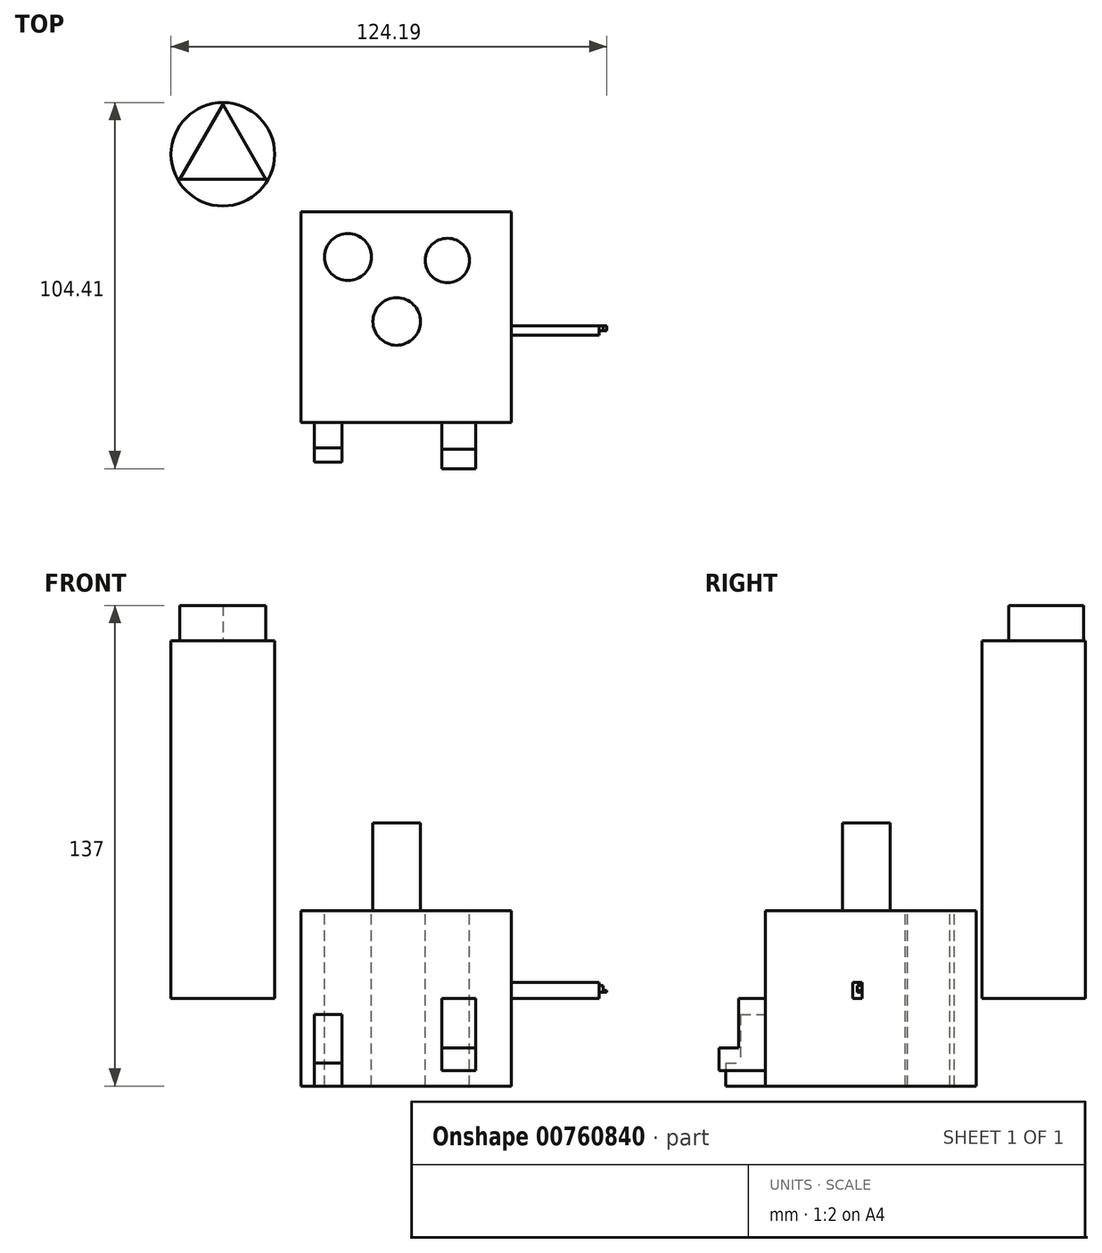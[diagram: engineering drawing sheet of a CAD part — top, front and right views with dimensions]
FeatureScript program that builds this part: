
annotation { "Feature Type Name" : "Feature", "Feature Type Description" : "" }
export const myFeature = defineFeature(function(context is Context, id is Id, definition is map)
    precondition{}
    {
        {
            var Q0;
            Q0=qCreatedBy(makeId("Top.planeOp"),FACE);
            var sketch = newSketch(context, id + "F0", { "sketchPlane" : qUnion([Q0])});
            skLineSegment(sketch, "E0.bottom", {"start": v(-27.3, 39.4) * mm, "end": v(32.7, 39.4) * mm});
            skLineSegment(sketch, "E0.top", {"start": v(-27.3, -20.6) * mm, "end": v(32.7, -20.6) * mm});
            skLineSegment(sketch, "E0.left", {"start": v(-27.3, 39.4) * mm, "end": v(-27.3, -20.6) * mm});
            skLineSegment(sketch, "E0.right", {"start": v(32.7, 39.4) * mm, "end": v(32.7, -20.6) * mm});
            skCircle(sketch, "E1", {"center": v(-13.9, 26.54) * mm, "radius": 6.7 * mm});
            skCircle(sketch, "E2", {"center": v(14.47, 25.58) * mm, "radius": 6.33 * mm});
            skArc(sketch, "E3", {"start": v(-18.68, 5.08) * mm, "mid": v(0.27, -16.23) * mm, "end": v(19.64, 4.7) * mm});
            skSolve(sketch);
        }
        {
            var Q0;
            Q0=makeQuery(id+"F0.imprint","IMPRINT",FACE,{"disambiguationData":[TD([[makeQuery(id+"F0.imprint","IMPRINT",EDGE,{"derivedFrom":sQuery(id+"F0.wireOp",EDGE,"E0.bottom")}),-1.0]])]});
            extrude(context, id + "F1", {"entities" : qUnion([Q0]), "oppositeDirection" : true, "depth" : 25 * mm, "offsetDistance" : 25 * mm});
        }
        {
            var Q0;
            Q0=makeQuery(id+"F1.opExtrude","CAP_FACE",FACE,{"disambiguationData":[OSD([sQuery(id+"F0.wireOp",EDGE,"E0.bottom"),sQuery(id+"F0.wireOp",EDGE,"E0.top"),sQuery(id+"F0.wireOp",EDGE,"E0.left"),sQuery(id+"F0.wireOp",EDGE,"E0.right")])],"isStart":false});
            extrude(context, id + "F2", {"entities" : qUnion([Q0]), "operationType" : NewBodyOperationType.ADD, "oppositeDirection" : true, "depth" : 1.1 * mm, "offsetDistance" : 25 * mm});
        }
        {
            var Q0;
            {var subQ0=sQuery(id+"F0.wireOp",EDGE,"E0.top");Q0=makeQuery(id+"F2.boolean.opBoolean","MERGE",FACE,{"derivedFrom":[makeQuery(id+"F1.opExtrude","SWEPT_FACE",FACE,{"disambiguationData":[OSD([subQ0])]}),makeQuery(id+"F2.opExtrude","SWEPT_FACE",FACE,{"disambiguationData":[OSD([subQ0])]})]});}
            extrude(context, id + "F3", {"entities" : qUnion([Q0]), "operationType" : NewBodyOperationType.ADD, "oppositeDirection" : true, "depth" : 25 * mm, "offsetDistance" : 25 * mm});
        }
        {
            var Q0;
            Q0 = qSketchRegion(id + "F0", true);
            extrude(context, id + "F4", {"entities" : qUnion([Q0]), "operationType" : NewBodyOperationType.ADD, "depth" : 25 * mm, "offsetDistance" : 25 * mm});
        }
        {
            var Q0;
            Q0=makeQuery(id+"F4.opExtrude","CAP_FACE",FACE,{"disambiguationData":[OSD([sQuery(id+"F0.wireOp",EDGE,"E0.bottom"),sQuery(id+"F0.wireOp",EDGE,"E0.top"),sQuery(id+"F0.wireOp",EDGE,"E0.left"),sQuery(id+"F0.wireOp",EDGE,"E0.right"),sQuery(id+"F0.wireOp",EDGE,"E1"),sQuery(id+"F0.wireOp",EDGE,"E2")])],"isStart":false});
            var sketch = newSketch(context, id + "F5", { "sketchPlane" : qUnion([Q0])});
            skCircle(sketch, "E4", {"center": v(0, 8.17) * mm, "radius": 6.77 * mm});
            skSolve(sketch);
        }
        {
            var Q0;
            Q0=makeQuery(id+"F5.imprint","IMPRINT",FACE,{"disambiguationData":[TD([[makeQuery(id+"F5.imprint","IMPRINT",EDGE,{"derivedFrom":sQuery(id+"F5.wireOp",EDGE,"E4")}),1.0]])]});
            extrude(context, id + "F6", {"entities" : qUnion([Q0]), "operationType" : NewBodyOperationType.ADD, "depth" : 25 * mm, "offsetDistance" : 25 * mm});
        }
        {
            var Q0;
            {var subQ0=sQuery(id+"F0.wireOp",EDGE,"E0.top");Q0=makeQuery(id+"F4.boolean.opBoolean","MERGE",FACE,{"derivedFrom":[makeQuery(id+"F1.opExtrude","SWEPT_FACE",FACE,{"disambiguationData":[OSD([subQ0])]}),makeQuery(id+"F4.opExtrude","SWEPT_FACE",FACE,{"disambiguationData":[OSD([subQ0])]})]});}
            var sketch = newSketch(context, id + "F7", { "sketchPlane" : qUnion([Q0])});
            skLineSegment(sketch, "E5.bottom", {"start": v(12.88, 0) * mm, "end": v(22.48, 0) * mm});
            skLineSegment(sketch, "E5.top", {"start": v(12.88, -20.6) * mm, "end": v(22.48, -20.6) * mm});
            skLineSegment(sketch, "E5.left", {"start": v(12.88, 0) * mm, "end": v(12.88, -20.6) * mm});
            skLineSegment(sketch, "E5.right", {"start": v(22.48, 0) * mm, "end": v(22.48, -20.6) * mm});
            skSolve(sketch);
        }
        {
            var Q0;
            Q0 = qSketchRegion(id + "F7", true);
            extrude(context, id + "F8", {"entities" : qUnion([Q0]), "operationType" : NewBodyOperationType.ADD, "depth" : 7.7 * mm, "offsetDistance" : 25 * mm});
        }
        {
            var Q0;
            Q0=makeQuery(id+"F8.opExtrude","CAP_FACE",FACE,{"disambiguationData":[OSD([sQuery(id+"F7.wireOp",EDGE,"E5.bottom"),sQuery(id+"F7.wireOp",EDGE,"E5.top"),sQuery(id+"F7.wireOp",EDGE,"E5.left"),sQuery(id+"F7.wireOp",EDGE,"E5.right")])],"isStart":false});
            var sketch = newSketch(context, id + "F9", { "sketchPlane" : qUnion([Q0])});
            skLineSegment(sketch, "E6.bottom", {"start": v(12.88, -14.07) * mm, "end": v(22.48, -14.07) * mm});
            skLineSegment(sketch, "E6.top", {"start": v(12.88, -20.6) * mm, "end": v(22.48, -20.6) * mm});
            skLineSegment(sketch, "E6.left", {"start": v(12.88, -14.07) * mm, "end": v(12.88, -20.6) * mm});
            skLineSegment(sketch, "E6.right", {"start": v(22.48, -14.07) * mm, "end": v(22.48, -20.6) * mm});
            skSolve(sketch);
        }
        {
            var Q0;
            Q0 = qSketchRegion(id + "F9", true);
            extrude(context, id + "F10", {"entities" : qUnion([Q0]), "operationType" : NewBodyOperationType.ADD, "depth" : 5.5 * mm, "offsetDistance" : 25 * mm});
        }
        {
            var Q0;
            {var subQ0=sQuery(id+"F0.wireOp",EDGE,"E0.top");Q0=makeQuery(id+"F4.boolean.opBoolean","MERGE",FACE,{"derivedFrom":[makeQuery(id+"F1.opExtrude","SWEPT_FACE",FACE,{"disambiguationData":[OSD([subQ0])]}),makeQuery(id+"F4.opExtrude","SWEPT_FACE",FACE,{"disambiguationData":[OSD([subQ0])]})]});}
            var sketch = newSketch(context, id + "F11", { "sketchPlane" : qUnion([Q0])});
            skLineSegment(sketch, "E7.bottom", {"start": v(-23.4, -4.6) * mm, "end": v(-15.53, -4.6) * mm});
            skLineSegment(sketch, "E7.top", {"start": v(-23.4, -25) * mm, "end": v(-15.53, -25) * mm});
            skLineSegment(sketch, "E7.left", {"start": v(-23.4, -4.6) * mm, "end": v(-23.4, -25) * mm});
            skLineSegment(sketch, "E7.right", {"start": v(-15.53, -4.6) * mm, "end": v(-15.53, -25) * mm});
            skSolve(sketch);
        }
        {
            var Q0;
            Q0=makeQuery(id+"F11.imprint","IMPRINT",FACE,{"disambiguationData":[TD([[makeQuery(id+"F11.imprint","IMPRINT",EDGE,{"derivedFrom":sQuery(id+"F11.wireOp",EDGE,"E7.bottom")}),-1.0]])]});
            extrude(context, id + "F12", {"entities" : qUnion([Q0]), "operationType" : NewBodyOperationType.ADD, "depth" : 7.2 * mm, "offsetDistance" : 25 * mm});
        }
        {
            var Q0;
            Q0=makeQuery(id+"F12.opExtrude","CAP_FACE",FACE,{"disambiguationData":[OSD([sQuery(id+"F11.wireOp",EDGE,"E7.bottom"),sQuery(id+"F11.wireOp",EDGE,"E7.top"),sQuery(id+"F11.wireOp",EDGE,"E7.left"),sQuery(id+"F11.wireOp",EDGE,"E7.right")])],"isStart":false});
            var sketch = newSketch(context, id + "F13", { "sketchPlane" : qUnion([Q0])});
            skLineSegment(sketch, "E8.bottom", {"start": v(-23.4, -18.5) * mm, "end": v(-15.53, -18.5) * mm});
            skLineSegment(sketch, "E8.top", {"start": v(-23.4, -25) * mm, "end": v(-15.53, -25) * mm});
            skLineSegment(sketch, "E8.left", {"start": v(-23.4, -18.5) * mm, "end": v(-23.4, -25) * mm});
            skLineSegment(sketch, "E8.right", {"start": v(-15.53, -18.5) * mm, "end": v(-15.53, -25) * mm});
            skSolve(sketch);
        }
        {
            var Q0;
            Q0 = qSketchRegion(id + "F13", true);
            extrude(context, id + "F14", {"entities" : qUnion([Q0]), "operationType" : NewBodyOperationType.ADD, "depth" : 4.1 * mm, "offsetDistance" : 25 * mm});
        }
        {
            var Q0;
            {var subQ0=sQuery(id+"F0.wireOp",EDGE,"E0.right");Q0=makeQuery(id+"F4.boolean.opBoolean","MERGE",FACE,{"derivedFrom":[makeQuery(id+"F1.opExtrude","SWEPT_FACE",FACE,{"disambiguationData":[OSD([subQ0])]}),makeQuery(id+"F4.opExtrude","SWEPT_FACE",FACE,{"disambiguationData":[OSD([subQ0])]})]});}
            var sketch = newSketch(context, id + "F15", { "sketchPlane" : qUnion([Q0])});
            skLineSegment(sketch, "E9.bottom", {"start": v(4.27, 4.48) * mm, "end": v(6.93, 4.48) * mm});
            skLineSegment(sketch, "E9.top", {"start": v(4.27, 0) * mm, "end": v(6.93, 0) * mm});
            skLineSegment(sketch, "E9.left", {"start": v(4.27, 4.48) * mm, "end": v(4.27, 0) * mm});
            skLineSegment(sketch, "E9.right", {"start": v(6.93, 4.48) * mm, "end": v(6.93, 0) * mm});
            skSolve(sketch);
        }
        {
            var Q0;
            Q0 = qSketchRegion(id + "F15", true);
            extrude(context, id + "F16", {"entities" : qUnion([Q0]), "operationType" : NewBodyOperationType.ADD, "depth" : 25 * mm, "offsetDistance" : 25 * mm});
        }
        {
            var Q0;
            Q0=makeQuery(id+"F16.opExtrude","CAP_FACE",FACE,{"disambiguationData":[OSD([sQuery(id+"F15.wireOp",EDGE,"E9.bottom"),sQuery(id+"F15.wireOp",EDGE,"E9.top"),sQuery(id+"F15.wireOp",EDGE,"E9.left"),sQuery(id+"F15.wireOp",EDGE,"E9.right")])],"isStart":false});
            var sketch = newSketch(context, id + "F17", { "sketchPlane" : qUnion([Q0])});
            skPoint(sketch, "E10.firstSnap0", {"position": v(6.93, 2.24) * mm});
            skLineSegment(sketch, "E10.bottom", {"start": v(5.54, 2.24) * mm, "end": v(6.93, 2.24) * mm});
            skLineSegment(sketch, "E10.top", {"start": v(5.54, 1.7) * mm, "end": v(6.93, 1.7) * mm});
            skLineSegment(sketch, "E10.left", {"start": v(5.54, 2.24) * mm, "end": v(5.54, 1.7) * mm});
            skLineSegment(sketch, "E10.right", {"start": v(6.93, 2.24) * mm, "end": v(6.93, 1.7) * mm});
            skSolve(sketch);
        }
        {
            var Q0;
            Q0 = qSketchRegion(id + "F17", true);
            extrude(context, id + "F18", {"entities" : qUnion([Q0]), "operationType" : NewBodyOperationType.ADD, "depth" : 2.2 * mm, "offsetDistance" : 25 * mm});
        }
        {
            var Q0;
            Q0=makeQuery(id+"F16.opExtrude","CAP_FACE",FACE,{"disambiguationData":[OSD([sQuery(id+"F15.wireOp",EDGE,"E9.bottom"),sQuery(id+"F15.wireOp",EDGE,"E9.top"),sQuery(id+"F15.wireOp",EDGE,"E9.left"),sQuery(id+"F15.wireOp",EDGE,"E9.right")])],"isStart":false});
            var sketch = newSketch(context, id + "F19", { "sketchPlane" : qUnion([Q0])});
            skLineSegment(sketch, "E11.bottom", {"start": v(5.54, 3.67) * mm, "end": v(6.93, 3.67) * mm});
            skLineSegment(sketch, "E11.top", {"start": v(5.54, 2.24) * mm, "end": v(6.93, 2.24) * mm});
            skLineSegment(sketch, "E11.left", {"start": v(5.54, 3.67) * mm, "end": v(5.54, 2.24) * mm});
            skLineSegment(sketch, "E11.right", {"start": v(6.93, 3.67) * mm, "end": v(6.93, 2.24) * mm});
            skSolve(sketch);
        }
        {
            var Q0;
            Q0 = qSketchRegion(id + "F19", true);
            extrude(context, id + "F20", {"entities" : qUnion([Q0]), "operationType" : NewBodyOperationType.ADD, "depth" : 1.2 * mm, "offsetDistance" : 25 * mm});
        }
        {
            var Q0;
            Q0=qCreatedBy(makeId("Top.planeOp"),FACE);
            var sketch = newSketch(context, id + "F21", { "sketchPlane" : qUnion([Q0])});
            skCircle(sketch, "E12", {"center": v(-49.53, 55.85) * mm, "radius": 14.75 * mm});
            skSolve(sketch);
        }
        {
            var Q0;
            Q0 = qSketchRegion(id + "F21", true);
            extrude(context, id + "F22", {"entities" : qUnion([Q0]), "depth" : 102 * mm, "offsetDistance" : 25 * mm});
        }
        {
            var Q0;
            Q0=makeQuery(id+"F22.opExtrude","CAP_FACE",FACE,{"disambiguationData":[OSD([sQuery(id+"F21.wireOp",EDGE,"E12")])],"isStart":false});
            var sketch = newSketch(context, id + "F23", { "sketchPlane" : qUnion([Q0])});
            skCircle(sketch, "E13.cCircle", {"center": v(-49.53, 55.85) * mm, "radius": 7.08 * mm, "construction": true});
            skLineSegment(sketch, "E13.0", {"start": v(-37.26, 48.77) * mm, "end": v(-61.8, 48.77) * mm});
            skLineSegment(sketch, "E13.1", {"start": v(-61.8, 48.77) * mm, "end": v(-49.53, 70.02) * mm});
            skLineSegment(sketch, "E13.2", {"start": v(-49.53, 70.02) * mm, "end": v(-37.26, 48.77) * mm});
            skPoint(sketch, "E13.0.midPoint", {"position": v(-49.53, 48.77) * mm});
            skSolve(sketch);
        }
        {
            var Q0;
            Q0 = qSketchRegion(id + "F23", true);
            extrude(context, id + "F24", {"entities" : qUnion([Q0]), "operationType" : NewBodyOperationType.ADD, "depth" : 10 * mm, "offsetDistance" : 25 * mm});
        }
    });
